FCSTD DOCUMENT  (FreeCAD 0.16R6706 (Git))
Label: rpcameraholder
License: All rights reserved
LicenseURL: http://en.wikipedia.org/wiki/All_rights_reserved
objects: Part::Box×6, Mesh::Feature×2, Part::Sphere×2, Part::Cut×2, Sketcher::SketchObject×2, PartDesign::Pocket×2, Part::Thickness×1, Part::MultiFuse×1, Part::Cylinder×1
note: 19 computed .brp shape members not serialized (recipe doc carries the construction recipe); baked Part::Feature solids carry a one-line shape summary decoded from their .brp

FEATURE [Mesh::Feature] BallJoint_Ball  label="BallJoint-Ball"
FEATURE [Mesh::Feature] BallJoint_Socket  label="BallJoint-Socket"
FEATURE [Part::Box] Box  label="Cube"
  Height = 1
  Length = 30
  Placement = pos=(-15,-6,-10) rot=(0,0,1;0rad)
  Width = 12
FEATURE [Part::Sphere] Sphere
  Angle1 = -90
  Angle2 = 90
  Angle3 = 360
  Radius = 10
FEATURE [Part::Box] Box001  label="Cube001"
  Height = 20
  Length = 20
  Placement = pos=(-10,-10,6) rot=(0,0,1;0rad)
  Width = 20
FEATURE [Part::Box] Box002  label="Cube002"
  Height = 10
  Length = 10
  Width = 10
FEATURE [Part::Cut] Cut
  Base = -> Sphere
  Tool = -> Box001
FEATURE [Part::Thickness] Thickness
  Faces = -> Cut [Face2]
  Intersection = false
  Join = 2
  Mode = 0
  SelfIntersection = false
  Value = -1
FEATURE [Part::Box] Box003  label="Cube003"
  Height = 20
  Length = 6
  Placement = pos=(-3,-10,-4) rot=(0,0,1;0rad)
  Width = 20
FEATURE [Part::Box] Box004  label="Cube004"
  Height = 20
  Length = 6
  Placement = pos=(10,-3,-4) rot=(0,0,1;1.5708rad)
  Width = 20
FEATURE [Part::MultiFuse] Fusion
  Shapes = -> [Box003,Box004]
FEATURE [Part::Cut] Cut001
  Base = -> Thickness
  Tool = -> Fusion
FEATURE [Sketcher::SketchObject] Sketch
  Placement = pos=(-15,-6,-9) rot=(0,0,1;0rad)
  Support = -> Box [Face6]
  sketch-geometry (2):
    g0: Circle CenterX=3.4 CenterY=6 CenterZ=0 NormalX=0 NormalY=0 NormalZ=1 Radius=1.6
    g1: Circle CenterX=26.9 CenterY=6 CenterZ=0 NormalX=0 NormalY=0 NormalZ=1 Radius=1.6
  constraints (6):
    c: DistanceX(g0,g1) = 23.5
    c: DistanceY(g1,g0) = 0
    c: Radius(g0) = 1.6
    c: Equal(g0,g1)
    c: DistanceX(g0) = 3.4
    c: DistanceY(g0) = 6
FEATURE [PartDesign::Pocket] Pocket
  Length = 5
  Placement = pos=(-15,-6,-10) rot=(0,0,1;0rad)
  Sketch = -> Sketch
  Type = 1
FEATURE [Part::Sphere] Sphere001
  Angle1 = -90
  Angle2 = 90
  Angle3 = 360
  Radius = 8.8
FEATURE [Part::Cylinder] Cylinder
  Angle = 360
  Height = 15
  Placement = pos=(0,0,8) rot=(0,0,1;0rad)
  Radius = 3
FEATURE [Part::Box] Box005  label="Cube005"
  Height = 30
  Length = 26
  Placement = pos=(-13,-3,18) rot=(0,0,1;0rad)
  Width = 2
FEATURE [Sketcher::SketchObject] Sketch001
  Placement = pos=(-13,-3,18) rot=(1,0,0;1.5708rad)
  Support = -> Box005 [Face3]
  sketch-geometry (10):
    g0: LineSegment StartX=0 StartY=19 StartZ=0 EndX=5.5 EndY=19 EndZ=0
    g1: LineSegment StartX=5.5 StartY=19 StartZ=0 EndX=5.5 EndY=9 EndZ=0
    g2: LineSegment StartX=5.5 StartY=9 StartZ=0 EndX=20.5 EndY=9 EndZ=0
    g3: LineSegment StartX=20.5 StartY=9 StartZ=0 EndX=20.5 EndY=19 EndZ=0
    g4: LineSegment StartX=20.5 StartY=19 StartZ=0 EndX=26 EndY=19 EndZ=0
    g5: LineSegment StartX=26 StartY=19 StartZ=0 EndX=26 EndY=30 EndZ=0
    g6: LineSegment StartX=26 StartY=30 StartZ=0 EndX=0 EndY=30 EndZ=0
    g7: LineSegment StartX=0 StartY=30 StartZ=0 EndX=0 EndY=19 EndZ=0
    g8: Circle CenterX=2.63652 CenterY=15 CenterZ=0 NormalX=0 NormalY=0 NormalZ=1 Radius=1.1
    g9: Circle CenterX=23.2365 CenterY=15 CenterZ=0 NormalX=0 NormalY=0 NormalZ=1 Radius=1.1
  constraints (30):
    c: PointOnObject(g0,g-2)
    c: Coincident(g0,g1)
    c: Vertical(g1)
    c: Coincident(g1,g2)
    c: Horizontal(g2)
    c: Coincident(g2,g3)
    c: Coincident(g3,g4)
    c: Horizontal(g4)
    c: Coincident(g4,g5)
    c: Vertical(g5)
    c: Coincident(g5,g6)
    c: Horizontal(g6)
    c: Coincident(g6,g7)
    c: Coincident(g7,g0)
    c: Vertical(g7)
    c: Vertical(g3)
    c: Horizontal(g0)
    c: Equal(g7,g5)
    c: Equal(g1,g3)
    c: Equal(g0,g4)
    c: DistanceX(g5) = 26
    c: DistanceY(g5) = 30
    c: DistanceY(g1) = 9
    c: DistanceY(g1,g1) = 10
    c: DistanceY(g8) = 15
    c: Radius(g8) = 1.1
    c: Equal(g9,g8)
    c: DistanceY(g9,g8) = 0
    c: DistanceX(g8,g9) = 20.6
    c: DistanceX(g2,g2) = 15
FEATURE [PartDesign::Pocket] Pocket001
  Length = 5
  Placement = pos=(-13,-3,18) rot=(0,0,1;0rad)
  Sketch = -> Sketch001
  Type = 1
